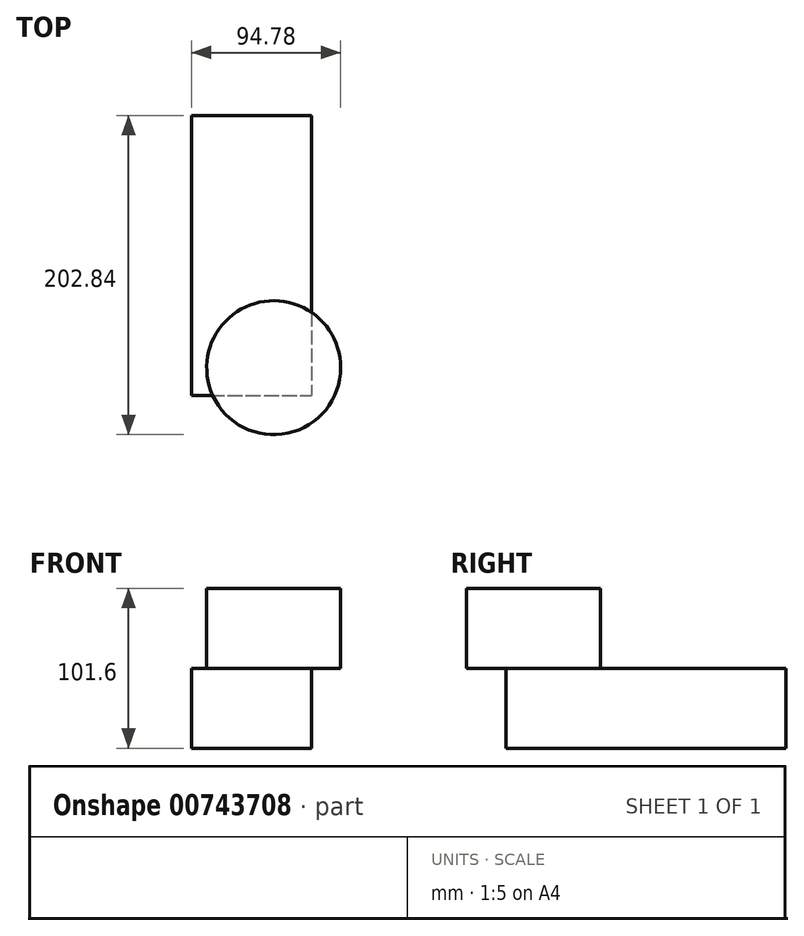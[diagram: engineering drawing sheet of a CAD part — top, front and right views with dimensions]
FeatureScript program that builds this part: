
annotation { "Feature Type Name" : "Feature", "Feature Type Description" : "" }
export const myFeature = defineFeature(function(context is Context, id is Id, definition is map)
    precondition{}
    {
        {
            var Q0;
            Q0=qCreatedBy(makeId("Top.planeOp"),FACE);
            var sketch = newSketch(context, id + "F0", { "sketchPlane" : qUnion([Q0])});
            skLineSegment(sketch, "E0.bottom", {"start": v(-51.01, 84.65) * mm, "end": v(25.19, 84.65) * mm});
            skLineSegment(sketch, "E0.top", {"start": v(-51.01, -93.15) * mm, "end": v(25.19, -93.15) * mm});
            skLineSegment(sketch, "E0.left", {"start": v(-51.01, 84.65) * mm, "end": v(-51.01, -93.15) * mm});
            skLineSegment(sketch, "E0.right", {"start": v(25.19, 84.65) * mm, "end": v(25.19, -93.15) * mm});
            skSolve(sketch);
        }
        {
            var Q0;
            Q0 = qSketchRegion(id + "F0", true);
            extrude(context, id + "F1", {"entities" : qUnion([Q0]), "depth" : 25.4 * mm, "offsetDistance" : 25.4 * mm});
        }
        {
            var Q0;
            Q0=makeQuery(id+"F1.opExtrude","CAP_FACE",FACE,{"disambiguationData":[OSD([sQuery(id+"F0.wireOp",EDGE,"E0.bottom"),sQuery(id+"F0.wireOp",EDGE,"E0.top"),sQuery(id+"F0.wireOp",EDGE,"E0.left"),sQuery(id+"F0.wireOp",EDGE,"E0.right")])],"isStart":false});
            extrude(context, id + "F2", {"entities" : qUnion([Q0]), "operationType" : NewBodyOperationType.ADD, "depth" : 25.4 * mm, "offsetDistance" : 25.4 * mm});
        }
        {
            var Q0;
            Q0=makeQuery(id+"F2.opExtrude","CAP_FACE",FACE,{"disambiguationData":[OSD([sQuery(id+"F0.wireOp",EDGE,"E0.bottom"),sQuery(id+"F0.wireOp",EDGE,"E0.top"),sQuery(id+"F0.wireOp",EDGE,"E0.left"),sQuery(id+"F0.wireOp",EDGE,"E0.right")])],"isStart":false});
            var sketch = newSketch(context, id + "F3", { "sketchPlane" : qUnion([Q0])});
            skSolve(sketch);
        }
        {
            var Q0;
            Q0=makeQuery(id+"F3.imprint","IMPRINT",FACE,{"disambiguationData":[TD([[makeQuery(id+"F3.imprint","IMPRINT",EDGE,{"derivedFrom":makeQuery(id+"F2.opExtrude","CAP_EDGE",EDGE,{"disambiguationData":[OSD([sQuery(id+"F0.wireOp",EDGE,"E0.bottom")])],"isStart":false})}),-1.0]])]});
            var sketch = newSketch(context, id + "F4", { "sketchPlane" : qUnion([Q0])});
            skCircle(sketch, "E1", {"center": v(1.23, -75.66) * mm, "radius": 42.54 * mm});
            skSolve(sketch);
        }
        {
            var Q0;
            Q0 = qSketchRegion(id + "F4", true);
            extrude(context, id + "F5", {"entities" : qUnion([Q0]), "operationType" : NewBodyOperationType.ADD, "depth" : 25.4 * mm, "offsetDistance" : 25.4 * mm});
        }
        {
            var Q0;
            Q0=makeQuery(id+"F5.opExtrude","CAP_FACE",FACE,{"disambiguationData":[OSD([sQuery(id+"F4.wireOp",EDGE,"E1")])],"isStart":false});
            extrude(context, id + "F6", {"entities" : qUnion([Q0]), "operationType" : NewBodyOperationType.ADD, "depth" : 25.4 * mm, "offsetDistance" : 25.4 * mm});
        }
    });
